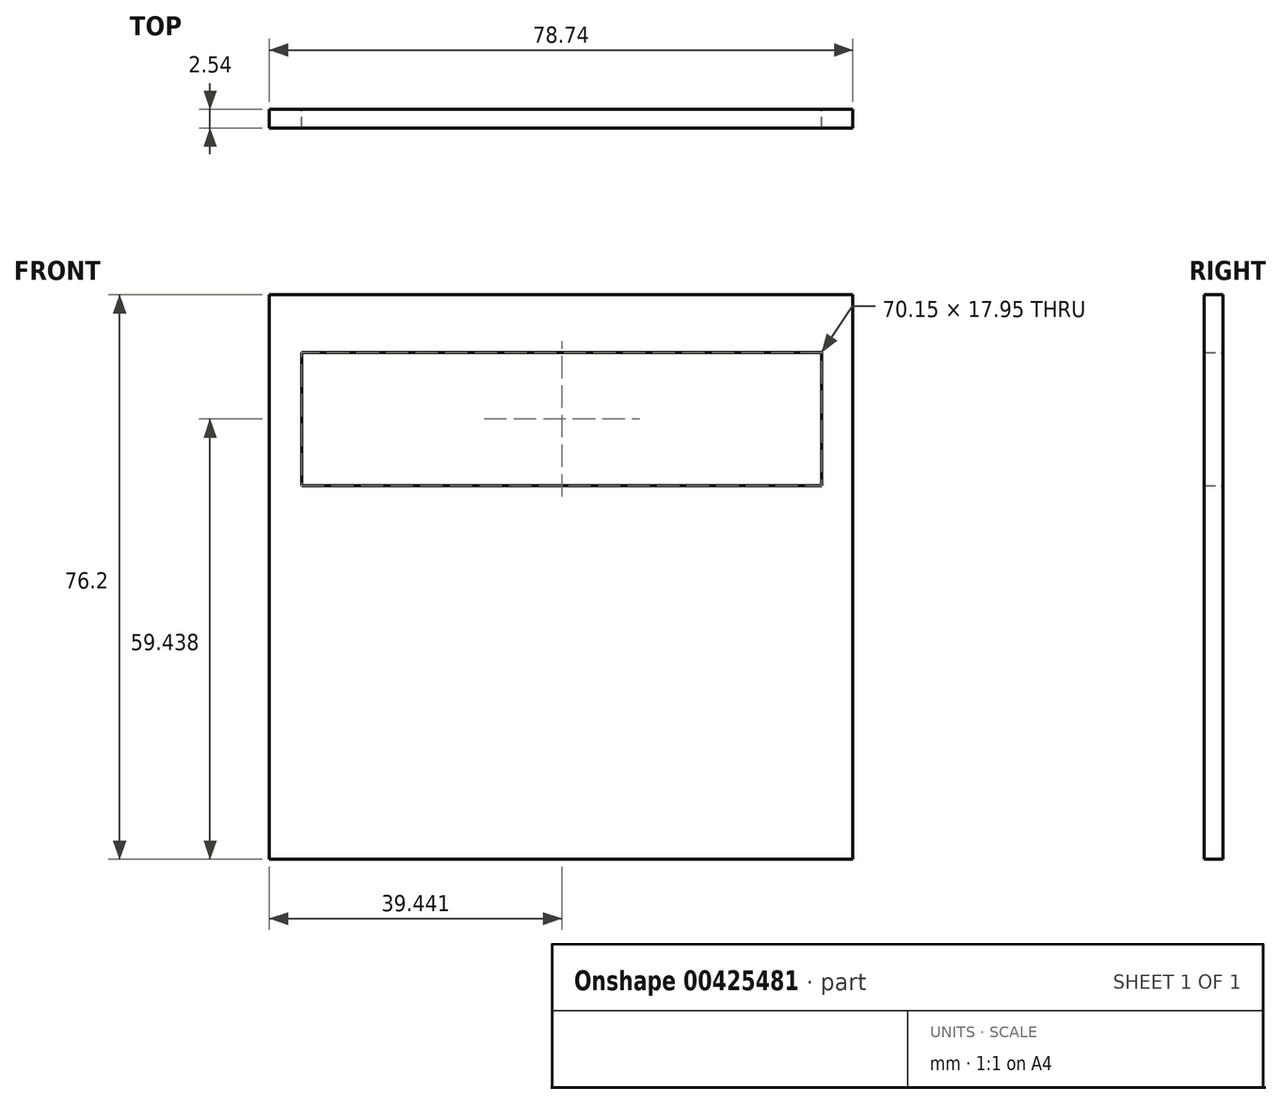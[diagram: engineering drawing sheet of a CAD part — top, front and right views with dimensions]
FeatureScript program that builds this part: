
annotation { "Feature Type Name" : "Feature", "Feature Type Description" : "" }
export const myFeature = defineFeature(function(context is Context, id is Id, definition is map)
    precondition{}
    {
        {
            var Q0;
            Q0=qCreatedBy(makeId("Front.planeOp"),FACE);
            var sketch = newSketch(context, id + "F0", { "sketchPlane" : qUnion([Q0])});
            skLineSegment(sketch, "E0.bottom", {"start": v(78.4, 78.82) * mm, "end": v(-0.34, 78.82) * mm});
            skLineSegment(sketch, "E0.top", {"start": v(78.4, 2.62) * mm, "end": v(-0.34, 2.62) * mm});
            skLineSegment(sketch, "E0.left", {"start": v(78.4, 78.82) * mm, "end": v(78.4, 2.62) * mm});
            skLineSegment(sketch, "E0.right", {"start": v(-0.34, 78.82) * mm, "end": v(-0.34, 2.62) * mm});
            skLineSegment(sketch, "E1.bottom", {"start": v(74.18, 71.03) * mm, "end": v(4.02, 71.03) * mm});
            skLineSegment(sketch, "E1.top", {"start": v(74.18, 53.08) * mm, "end": v(4.02, 53.08) * mm});
            skLineSegment(sketch, "E1.left", {"start": v(74.18, 71.03) * mm, "end": v(74.18, 53.08) * mm});
            skLineSegment(sketch, "E1.right", {"start": v(4.02, 71.03) * mm, "end": v(4.02, 53.08) * mm});
            skSolve(sketch);
        }
        {
            var Q0;
            Q0=makeQuery(id+"F0.imprint","IMPRINT",FACE,{"disambiguationData":[TD([[makeQuery(id+"F0.imprint","IMPRINT",EDGE,{"derivedFrom":sQuery(id+"F0.wireOp",EDGE,"E0.bottom")}),1.0]])]});
            extrude(context, id + "F1", {"entities" : qUnion([Q0]), "depth" : 2.54 * mm});
        }
    });
